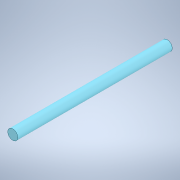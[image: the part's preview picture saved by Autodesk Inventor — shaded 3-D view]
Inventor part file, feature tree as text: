
AUTODESK INVENTOR PART (.ipt)
format: ipt  version: 2022 (Build 260153000, 153)  size: 102,400 bytes
history: native  units: in
note: dims shown in document units (in); Inventor stores cm internally (conversion verified against a paired STEP export)
features: extrude x1, sketch x1
ambient origin geometry x8: Origin, YZ Plane, XZ Plane, XY Plane, X Axis, Y Axis, Z Axis, Center Point
bodies: Solid1 (feature_tree)
feature tree (2):
  extrude  "Extrusion1"  Depth=3.937in
  sketch  "Sketch2"  dims[d0=3.937in d1=0.0in d2=0.2559in]
